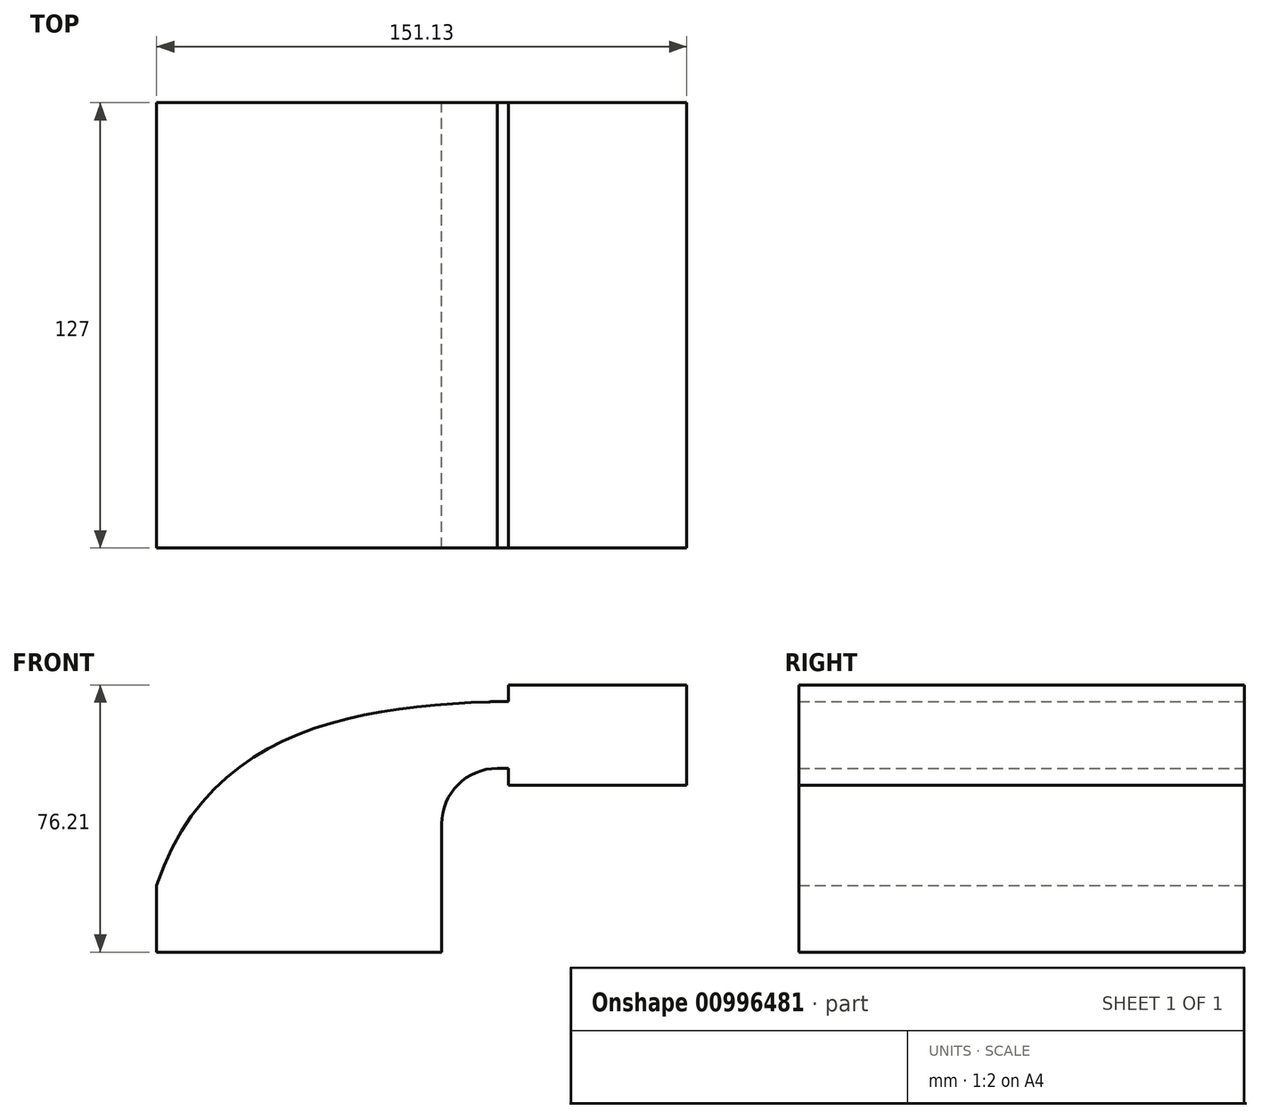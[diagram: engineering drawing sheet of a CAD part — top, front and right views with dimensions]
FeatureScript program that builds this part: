
annotation { "Feature Type Name" : "Feature", "Feature Type Description" : "" }
export const myFeature = defineFeature(function(context is Context, id is Id, definition is map)
    precondition{}
    {
        {
            var Q0;
            Q0=qCreatedBy(makeId("Front.planeOp"),FACE);
            var sketch = newSketch(context, id + "F0", { "sketchPlane" : qUnion([Q0])});
            skLineSegment(sketch, "E0.bottom", {"start": v(40.64, -9.52) * mm, "end": v(-40.64, -9.52) * mm});
            skLineSegment(sketch, "E0.top", {"start": v(40.64, 9.53) * mm, "end": v(-40.64, 9.53) * mm});
            skLineSegment(sketch, "E0.left", {"start": v(40.64, -9.52) * mm, "end": v(40.64, 9.53) * mm});
            skLineSegment(sketch, "E0.right", {"start": v(-40.64, -9.52) * mm, "end": v(-40.64, 9.53) * mm});
            skPoint(sketch, "E0.middle", {"position": v(0, 0) * mm});
            skLineSegment(sketch, "E1.bottom", {"start": v(110.5, 38.1) * mm, "end": v(59.7, 38.1) * mm});
            skLineSegment(sketch, "E1.top", {"start": v(110.5, 66.68) * mm, "end": v(59.7, 66.68) * mm});
            skLineSegment(sketch, "E1.left", {"start": v(110.5, 38.1) * mm, "end": v(110.5, 66.68) * mm});
            skLineSegment(sketch, "E1.right", {"start": v(59.7, 38.1) * mm, "end": v(59.7, 66.68) * mm});
            skPoint(sketch, "E1.middle", {"position": v(85.09, 52.39) * mm});
            skLineSegment(sketch, "E2", {"start": v(40.64, 9.53) * mm, "end": v(40.64, 27) * mm});
            skArc(sketch, "E3", {"start": v(40.64, 27) * mm, "mid": v(45.29, 38.23) * mm, "end": v(56.52, 42.88) * mm});
            skLineSegment(sketch, "E4", {"start": v(56.52, 42.88) * mm, "end": v(84.3, 42.88) * mm});
            skLineSegment(sketch, "E5.0", {"start": v(56.52, 61.93) * mm, "end": v(84.3, 61.93) * mm});
            skArc(sketch, "E5.1", {"start": v(21.6, 27) * mm, "mid": v(31.82, 51.7) * mm, "end": v(56.52, 61.93) * mm});
            skLineSegment(sketch, "E5.2", {"start": v(21.59, 9.53) * mm, "end": v(21.59, 27) * mm});
            skLineSegment(sketch, "E6", {"start": v(84.3, 38.1) * mm, "end": v(84.3, 66.68) * mm});
            skPoint(sketch, "E6.startSnap0", {"position": v(85.1, 38.1) * mm});
            skFitSpline(sketch, "E7", {"points": [v(-40.64, 9.52) * mm, v(56.52, 61.93) * mm], "startDerivative": vector(45.49, 134.61) * mm, "endDerivative": vector(120.61, 3.86) * mm});
            skSolve(sketch);
        }
        {
            var Q0;
            {var subQ0=sQuery(id+"F0.wireOp",EDGE,"E7");var subQ1=sQuery(id+"F0.wireOp",EDGE,"E5.1");var subQ3=makeQuery(id+"F0.imprint","INTERSECT",VERTEX,{"derivedFrom":[subQ1,subQ0]});Q0=makeQuery(id+"F0.imprint","IMPRINT",FACE,{"disambiguationData":[TD([[makeQuery(id+"F0.imprint","IMPRINT",EDGE,{"disambiguationData":[TD([[subQ3,-1.0]])],"derivedFrom":subQ1}),-1.0]])]});}
            var Q1;
            Q1=makeQuery(id+"F0.imprint","IMPRINT",FACE,{"disambiguationData":[TD([[makeQuery(id+"F0.imprint","IMPRINT",EDGE,{"derivedFrom":sQuery(id+"F0.wireOp",EDGE,"E0.bottom")}),-1.0]])]});
            var Q2;
            {var subQ0=sQuery(id+"F0.wireOp",EDGE,"E1.right");var subQ1=sQuery(id+"F0.wireOp",EDGE,"E1.bottom");var subQ2=makeQuery(id+"F0.imprint","INTERSECT",VERTEX,{"derivedFrom":[subQ1,subQ0]});Q2=makeQuery(id+"F0.imprint","IMPRINT",FACE,{"disambiguationData":[TD([[makeQuery(id+"F0.imprint","IMPRINT",EDGE,{"disambiguationData":[TD([[subQ2,1.0]])],"derivedFrom":subQ1}),-1.0]])]});}
            var Q3;
            {var subQ0=sQuery(id+"F0.wireOp",EDGE,"E1.right");var subQ1=sQuery(id+"F0.wireOp",EDGE,"E1.top");var subQ2=makeQuery(id+"F0.imprint","INTERSECT",VERTEX,{"derivedFrom":[subQ1,subQ0]});Q3=makeQuery(id+"F0.imprint","IMPRINT",FACE,{"disambiguationData":[TD([[makeQuery(id+"F0.imprint","IMPRINT",EDGE,{"disambiguationData":[TD([[subQ2,1.0]])],"derivedFrom":subQ1}),1.0]])]});}
            var Q4;
            {var subQ0=sQuery(id+"F0.wireOp",EDGE,"E1.left");Q4=makeQuery(id+"F0.imprint","IMPRINT",FACE,{"disambiguationData":[TD([[makeQuery(id+"F0.imprint","IMPRINT",EDGE,{"derivedFrom":subQ0}),1.0]])]});}
            var Q5;
            {var subQ0=sQuery(id+"F0.wireOp",EDGE,"E4");var subQ1=sQuery(id+"F0.wireOp",EDGE,"E1.right");var subQ2=makeQuery(id+"F0.imprint","INTERSECT",VERTEX,{"derivedFrom":[subQ1,subQ0]});Q5=makeQuery(id+"F0.imprint","IMPRINT",FACE,{"disambiguationData":[TD([[makeQuery(id+"F0.imprint","IMPRINT",EDGE,{"disambiguationData":[TD([[subQ2,-1.0]])],"derivedFrom":subQ1}),-1.0]])]});}
            var Q6;
            {var subQ1=sQuery(id+"F0.wireOp",EDGE,"E2");Q6=makeQuery(id+"F0.imprint","IMPRINT",FACE,{"disambiguationData":[TD([[makeQuery(id+"F0.imprint","IMPRINT",EDGE,{"derivedFrom":subQ1}),1.0]])]});}
            extrude(context, id + "F1", {"entities" : qUnion([Q0, Q1, Q2, Q3, Q4, Q5, Q6]), "endBound" : BoundingType.SYMMETRIC, "depth" : 127 * mm, "offsetDistance" : 25.4 * mm});
        }
    });
